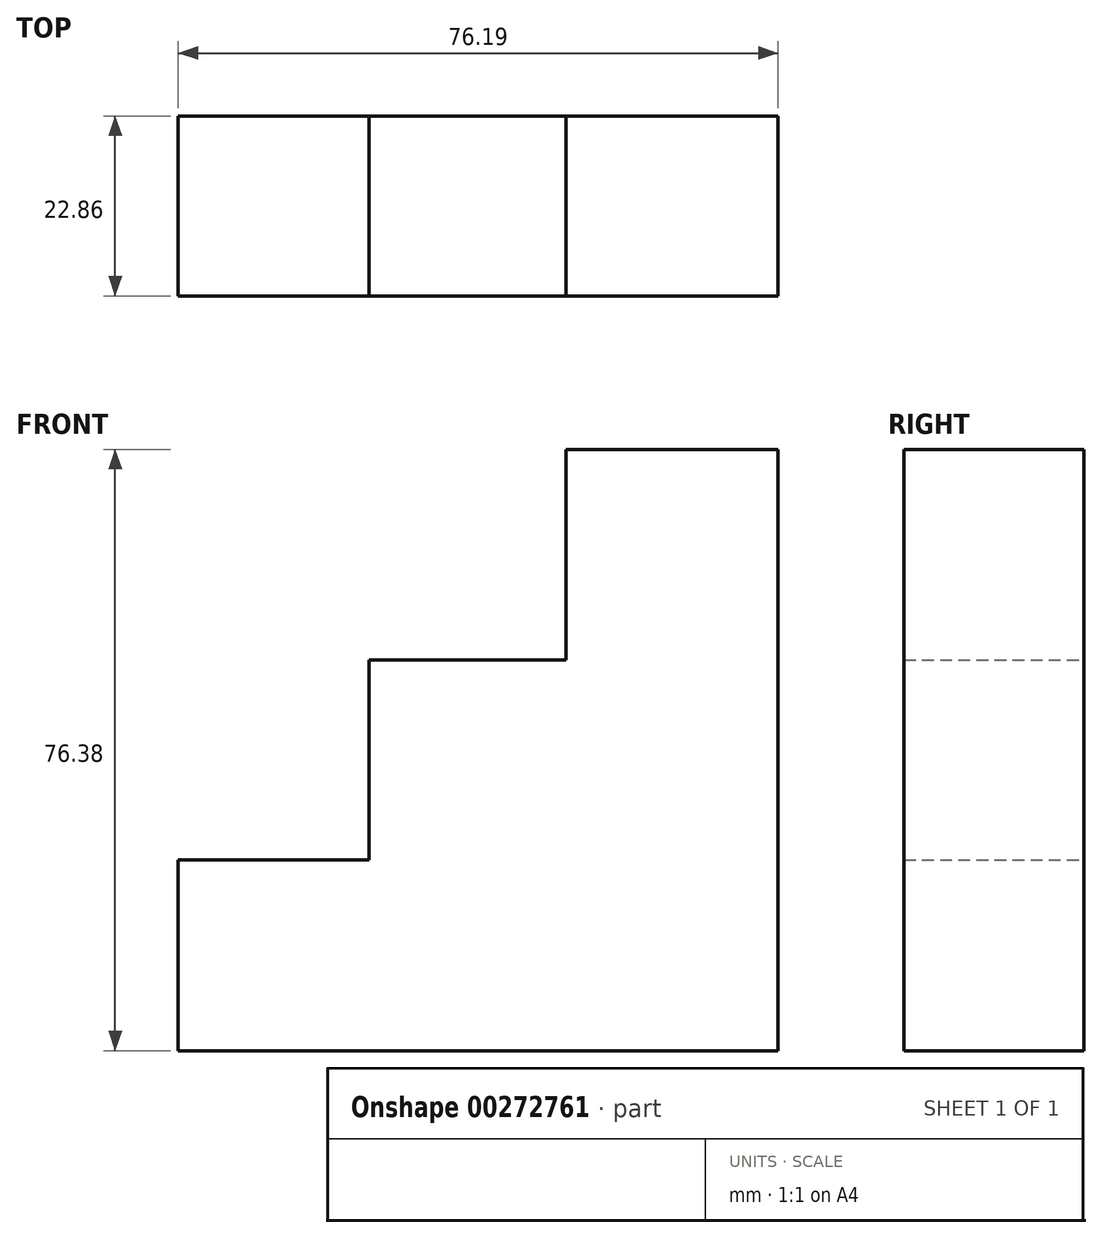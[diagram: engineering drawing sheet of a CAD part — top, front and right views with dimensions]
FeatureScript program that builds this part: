
annotation { "Feature Type Name" : "Feature", "Feature Type Description" : "" }
export const myFeature = defineFeature(function(context is Context, id is Id, definition is map)
    precondition{}
    {
        {
            var Q0;
            Q0=qCreatedBy(makeId("Front.planeOp"),FACE);
            var sketch = newSketch(context, id + "F0", { "sketchPlane" : qUnion([Q0])});
            skLineSegment(sketch, "E0", {"start": v(0, 0) * mm, "end": v(-76.2, 0) * mm});
            skLineSegment(sketch, "E1", {"start": v(-76.2, 0) * mm, "end": v(-76.2, 24.25) * mm});
            skLineSegment(sketch, "E2", {"start": v(-76.2, 24.25) * mm, "end": v(-51.94, 24.25) * mm});
            skLineSegment(sketch, "E3", {"start": v(-51.94, 24.25) * mm, "end": v(-51.94, 49.65) * mm});
            skLineSegment(sketch, "E4", {"start": v(-51.94, 49.65) * mm, "end": v(-26.93, 49.65) * mm});
            skLineSegment(sketch, "E5", {"start": v(-26.93, 49.65) * mm, "end": v(-26.93, 76.38) * mm});
            skLineSegment(sketch, "E6", {"start": v(-26.93, 76.38) * mm, "end": v(0, 76.38) * mm});
            skLineSegment(sketch, "E7", {"start": v(0, 76.38) * mm, "end": v(0, 0) * mm});
            skSolve(sketch);
        }
        {
            var Q0;
            Q0 = qSketchRegion(id + "F0", true);
            extrude(context, id + "F1", {"entities" : qUnion([Q0]), "depth" : 22.86 * mm});
        }
    });
